# Revit family: Emergency_Equipment-Haws_Corporation-Barrier_Free_Eye_Face_Wash_7656WCC new
name_source: partatom
category: Plumbing Fixtures
revit_build: Autodesk Revit Architecture 2015 (Build: 20160512_1515(x64)
units: mm (PartAtom-declared; Revit-internal decimal feet)

## types (1)
- 7656WCC
    Assembly Code = D2010610
    CW Connection = Yes
    CWFU = 1
    Cabinet = Metal - Haws Corporation - Stainless Steel - Bead Blast 300
    Cabinet Depth = 0' - 3 1/2"
    Cabinet Height = 2' - 8"
    Cabinet Width = 1' - 2"
    Cost = 0 $
    Cost Note = For Cost information please visit the Resource tab in the Product Page URL
    Default Elevation = 1' - 9 7/8"
    Description = Mounted within a recessed wall cabinet with drain pan
    Flow = 12 GPM
    HW Connection = No
    HWFU = 0
    Keynote = 15400
    Manufacturer = Haws Corporation
    Model = 7656WCC
    Product Documentation Link = https://www.hawsco.com
    Product Page URL = http://www.hawsco.com
    Sanitary Radius = 0' - 1"
    Series = Twin Feather-Flo® heads
    Spray Heads = Metal - Haws Corporation - Green Powder Coating
    Supply Radius = 0' - 0 1/4"
    Type Comments = For all users including wheel chair access
    URL = http://www.hawsco.com
    Vent Connection = No
    Version = 2014-v2.0a
    WFU = 1
    Waste Connection = Yes

## geometry (parser evidence)
native form markers: Blend x16, Sweep x7
no freeform markers — native parametric forms only
